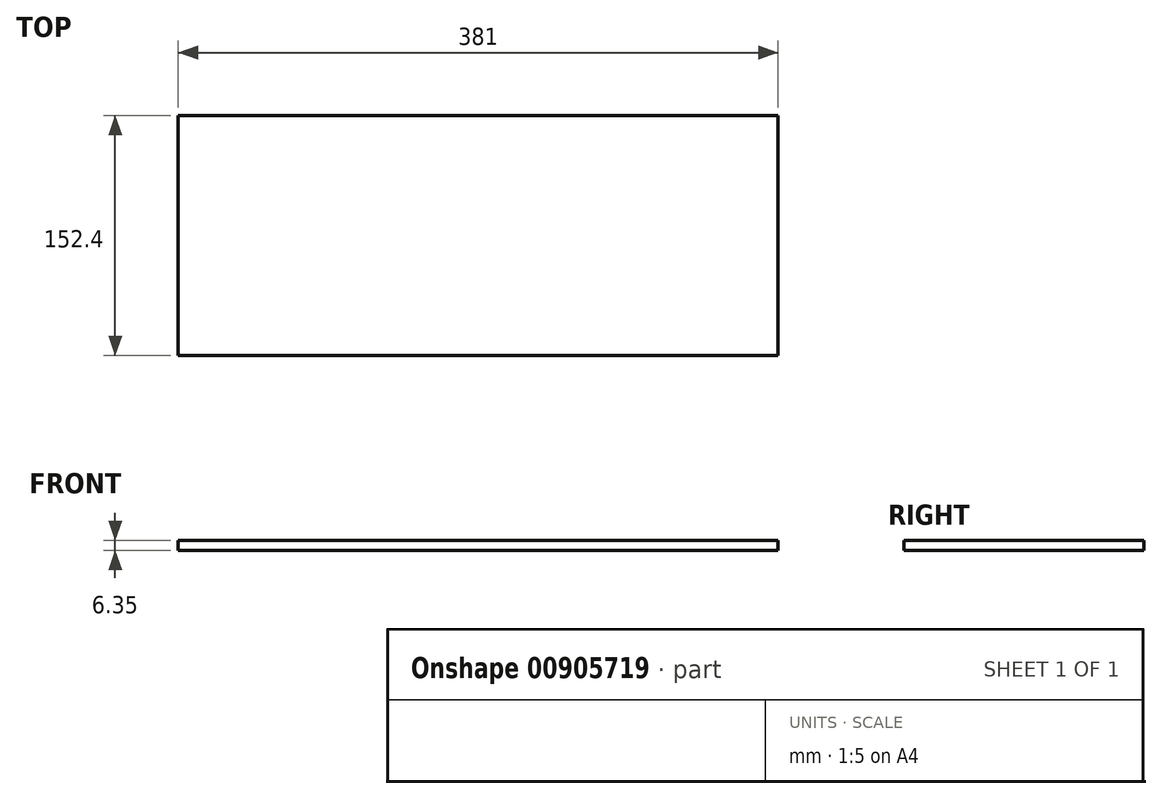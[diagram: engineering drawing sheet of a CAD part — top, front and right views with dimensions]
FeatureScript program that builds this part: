
annotation { "Feature Type Name" : "Feature", "Feature Type Description" : "" }
export const myFeature = defineFeature(function(context is Context, id is Id, definition is map)
    precondition{}
    {
        {
            var Q0;
            Q0=qCreatedBy(makeId("Front.planeOp"),FACE);
            var sketch = newSketch(context, id + "F0", { "sketchPlane" : qUnion([Q0])});
            skLineSegment(sketch, "E0.bottom", {"start": v(-192.13, -23.3) * mm, "end": v(188.87, -23.3) * mm});
            skLineSegment(sketch, "E0.top", {"start": v(-192.13, -29.65) * mm, "end": v(188.87, -29.65) * mm});
            skLineSegment(sketch, "E0.left", {"start": v(-192.13, -23.3) * mm, "end": v(-192.13, -29.65) * mm});
            skLineSegment(sketch, "E0.right", {"start": v(188.87, -23.3) * mm, "end": v(188.87, -29.65) * mm});
            skSolve(sketch);
        }
        {
            var Q0;
            Q0=makeQuery(id+"F0.imprint","IMPRINT",FACE,{"disambiguationData":[TD([[makeQuery(id+"F0.imprint","IMPRINT",EDGE,{"derivedFrom":sQuery(id+"F0.wireOp",EDGE,"E0.bottom")}),-1.0]])]});
            extrude(context, id + "F1", {"entities" : qUnion([Q0]), "depth" : 152.4 * mm, "offsetDistance" : 25.4 * mm});
        }
    });
